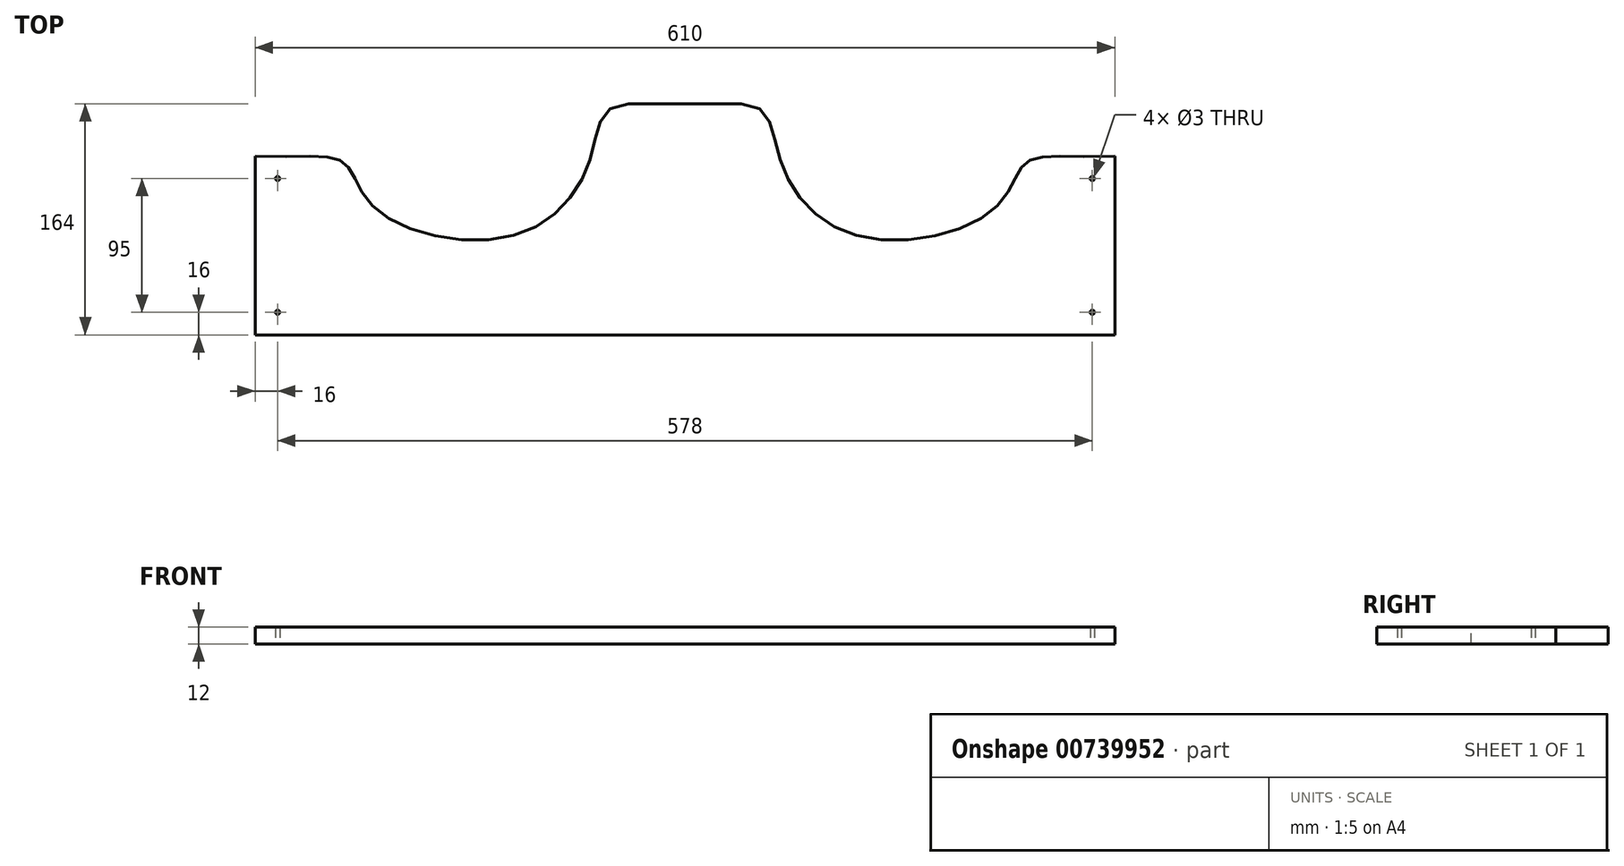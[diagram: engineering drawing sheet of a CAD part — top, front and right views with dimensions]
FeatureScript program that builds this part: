
annotation { "Feature Type Name" : "Feature", "Feature Type Description" : "" }
export const myFeature = defineFeature(function(context is Context, id is Id, definition is map)
    precondition{}
    {
        {
            var Q0;
            Q0=qCreatedBy(makeId("Top.planeOp"),FACE);
            var sketch = newSketch(context, id + "F0", { "sketchPlane" : qUnion([Q0])});
            skLineSegment(sketch, "E0.bottom", {"start": v(-305, 0) * mm, "end": v(305, 0) * mm});
            skLineSegment(sketch, "E0.top", {"start": v(-40, 164) * mm, "end": v(40, 164) * mm});
            skLineSegment(sketch, "E0.left", {"start": v(-305, 0) * mm, "end": v(-305, 127) * mm});
            skLineSegment(sketch, "E0.right", {"start": v(305, 0) * mm, "end": v(305, 127) * mm});
            skFitSpline(sketch, "E1", {"points": [v(-40, 164) * mm, v(-67.52, 124) * mm, v(-123.52, 70) * mm, v(-220.2, 90.1) * mm, v(-240.73, 121.15) * mm, v(-305, 127) * mm], "startDerivative": vector(-394.76, 0) * mm, "endDerivative": vector(-576.23, 21.18) * mm});
            skFitSpline(sketch, "E2.MirrorCS", {"points": [v(40, 164) * mm, v(67.52, 124) * mm, v(123.52, 70) * mm, v(220.2, 90.1) * mm, v(240.73, 121.15) * mm, v(305, 127) * mm], "startDerivative": vector(394.76, 0) * mm, "endDerivative": vector(576.23, 21.18) * mm});
            skLineSegment(sketch, "E3", {"start": v(-289, 126.67) * mm, "end": v(-289, 0) * mm, "construction": true});
            skCircle(sketch, "E4", {"center": v(-289, 16) * mm, "radius": 1.5 * mm});
            skCircle(sketch, "E5", {"center": v(-289, 111) * mm, "radius": 1.5 * mm});
            skCircle(sketch, "E6.MirrorC", {"center": v(289, 16) * mm, "radius": 1.5 * mm});
            skCircle(sketch, "E7.MirrorC", {"center": v(289, 111) * mm, "radius": 1.5 * mm});
            skLineSegment(sketch, "E8.MirrorCS", {"start": v(289, 126.67) * mm, "end": v(289, 0) * mm, "construction": true});
            skSolve(sketch);
        }
        {
            var Q0;
            Q0=makeQuery(id+"F0.imprint","IMPRINT",FACE,{"disambiguationData":[TD([[makeQuery(id+"F0.imprint","IMPRINT",EDGE,{"derivedFrom":sQuery(id+"F0.wireOp",EDGE,"E0.bottom")}),1.0]])]});
            extrude(context, id + "F1", {"entities" : qUnion([Q0]), "depth" : 12 * mm, "offsetDistance" : 25 * mm});
        }
    });
